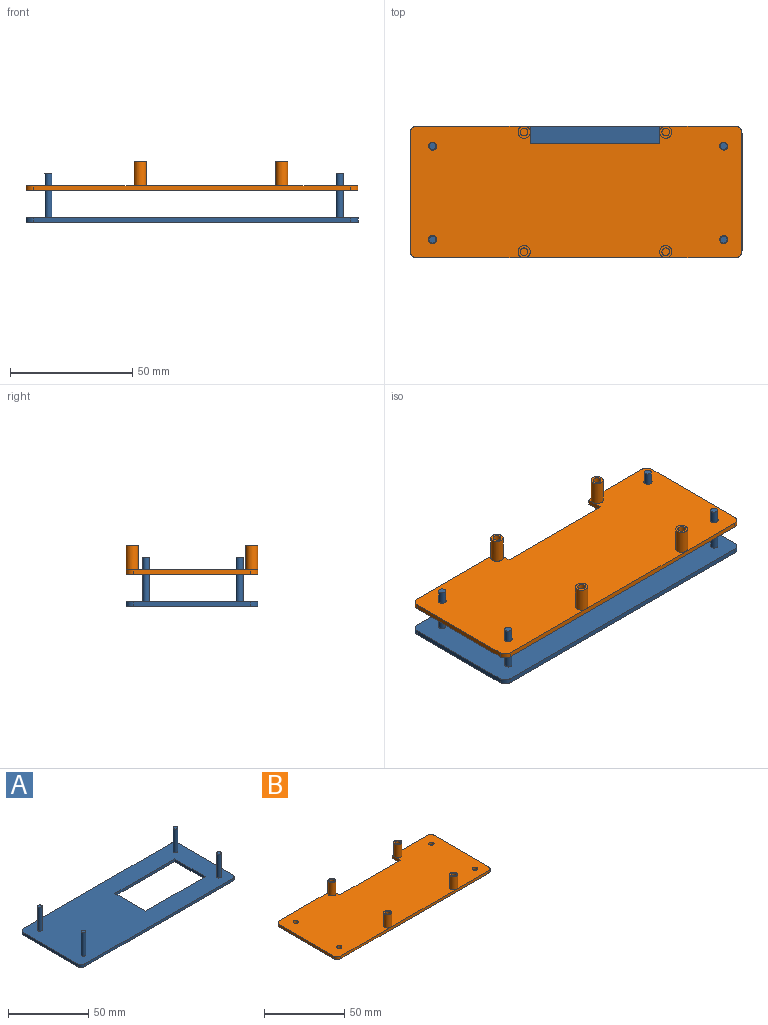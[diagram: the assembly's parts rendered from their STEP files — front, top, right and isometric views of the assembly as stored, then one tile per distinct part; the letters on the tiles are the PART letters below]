
ASSEMBLY  parts=2 mates=1
PART A: 22 faces, bbox 136x54x20 mm
  f0: plane 136x54mm, normal (0,0,1), area 5893.3mm2, adj f2,f3,f4,f5,f6,f8,f10,f12
  f1: plane 136x54mm, normal (0,0,-1), area 5918.8mm2, adj f2,f3,f4,f5,f14,f15,f16,f17
  f2: plane 130x2mm, normal (0,-1,0), area 260mm2, adj f0,f1,f18,f21
  f3: plane 48x2mm, normal (1,0,0), area 96mm2, adj f0,f1,f18,f19
  f4: plane 130x2mm, normal (0,1,0), area 260mm2, adj f0,f1,f19,f20
  f5: plane 48x2mm, normal (-1,0,0), area 96mm2, adj f0,f1,f20,f21
  f6: cylinder r=1.43mm len=18mm, axis (0,0,-1), area 161.2mm2, adj f0,f7
  f7: plane 2.85x2.85mm, normal (0,0,1), area 6.4mm2, adj f6
  f8: cylinder r=1.43mm len=18mm, axis (0,0,-1), area 161.2mm2, adj f0,f9
  f9: plane 2.85x2.85mm, normal (0,0,1), area 6.4mm2, adj f8
  f10: cylinder r=1.43mm len=18mm, axis (0,0,-1), area 161.2mm2, adj f0,f11
  f11: plane 2.85x2.85mm, normal (0,0,1), area 6.4mm2, adj f10
  f12: cylinder r=1.43mm len=18mm, axis (0,0,-1), area 161.2mm2, adj f0,f13
  f13: plane 2.85x2.85mm, normal (0,0,1), area 6.4mm2, adj f12
  f14: plane 52.5x2mm, normal (0,-1,0), area 105mm2, adj f0,f1,f15,f17
  f15: plane 27x2mm, normal (1,0,0), area 54mm2, adj f0,f1,f14,f16
  f16: plane 52.5x2mm, normal (0,1,0), area 105mm2, adj f0,f1,f15,f17
  f17: plane 27x2mm, normal (-1,0,0), area 54mm2, adj f0,f1,f14,f16
  f18: cylinder r=3mm len=3mm, axis (0,0,1), area 9.4mm2, adj f0,f1,f2,f3
  f19: cylinder r=3mm len=3mm, axis (0,0,-1), area 9.4mm2, adj f0,f1,f3,f4
  f20: cylinder r=3mm len=3mm, axis (0,0,1), area 9.4mm2, adj f0,f1,f4,f5
  f21: cylinder r=3mm len=3mm, axis (0,0,-1), area 9.4mm2, adj f0,f1,f2,f5
PART B: 36 faces, bbox 136x54x12 mm
  f0: plane 46.24x2mm, normal (0,1,0), area 92.5mm2, adj f1,f2,f3,f29,f34
  f1: plane 136x54mm, normal (0,0,1), area 6849.8mm2, adj f0,f5,f6,f7,f8,f10,f13,f18
  f2: plane 2.5x2.5mm, normal (0,0,1), area 1.3mm2, adj f0,f18,f29
  f3: plane 136x54mm, normal (0,0,-1), area 6931.1mm2, adj f0,f5,f6,f7,f8,f25,f26,f27
  f4: plane 2.5x2.5mm, normal (0,0,1), area 1.3mm2, adj f7,f13,f31
  f5: plane 130x2mm, normal (0,-1,0), area 260mm2, adj f1,f3,f32,f35
  f6: plane 48x2mm, normal (1,0,0), area 96mm2, adj f1,f3,f32,f33
  f7: plane 30.76x2mm, normal (0,1,0), area 61.5mm2, adj f1,f3,f4,f31,f33
  f8: plane 48x2mm, normal (-1,0,0), area 96mm2, adj f1,f3,f34,f35
  f9: cylinder r=1.57mm len=10mm, axis (0,0,-1), area 99mm2, adj f11,f12
  f10: cylinder r=2.5mm len=10mm, axis (0,0,-1), area 157.1mm2, adj f1,f11
  f11: plane 5x5mm, normal (0,0,1), area 11.8mm2, adj f9,f10
  f12: plane 3.15x3.15mm, normal (0,0,1), area 7.8mm2, adj f9
  f13: cylinder r=2.5mm len=10mm, axis (0,0,-1), area 157.1mm2, adj f1,f4,f15
  f14: cylinder r=1.57mm len=10mm, axis (0,0,-1), area 99mm2, adj f15,f16
  f15: plane 5x5mm, normal (0,0,1), area 11.8mm2, adj f13,f14
  f16: plane 3.15x3.15mm, normal (0,0,1), area 7.8mm2, adj f14
  f17: cylinder r=1.57mm len=10mm, axis (0,0,-1), area 99mm2, adj f19,f20
  f18: cylinder r=2.5mm len=10mm, axis (0,0,-1), area 157.1mm2, adj f1,f2,f19
  f19: plane 5x5mm, normal (0,0,1), area 11.8mm2, adj f17,f18
  f20: plane 3.15x3.15mm, normal (0,0,1), area 7.8mm2, adj f17
  f21: cylinder r=2.5mm len=10mm, axis (0,0,-1), area 157.1mm2, adj f1,f23
  f22: cylinder r=1.57mm len=10mm, axis (0,0,-1), area 99mm2, adj f23,f24
  f23: plane 5x5mm, normal (0,0,1), area 11.8mm2, adj f21,f22
  f24: plane 3.15x3.15mm, normal (0,0,1), area 7.8mm2, adj f22
  f25: cylinder r=1.65mm len=3.3mm, axis (0,0,1), area 20.7mm2, adj f1,f3
  f26: cylinder r=1.65mm len=3.3mm, axis (0,0,1), area 20.7mm2, adj f1,f3
  f27: cylinder r=1.65mm len=3.3mm, axis (0,0,1), area 20.7mm2, adj f1,f3
  f28: cylinder r=1.65mm len=3.3mm, axis (0,0,1), area 20.7mm2, adj f1,f3
  f29: plane 7x2mm, normal (1,0,0), area 14mm2, adj f0,f1,f2,f3,f30
  f30: plane 53x2mm, normal (0,1,0), area 106mm2, adj f1,f3,f29,f31
  f31: plane 7x2mm, normal (-1,0,0), area 14mm2, adj f1,f3,f4,f7,f30
  f32: cylinder r=3mm len=3mm, axis (0,0,1), area 9.4mm2, adj f1,f3,f5,f6
  f33: cylinder r=3mm len=3mm, axis (0,0,-1), area 9.4mm2, adj f1,f3,f6,f7
  f34: cylinder r=3mm len=3mm, axis (0,0,1), area 9.4mm2, adj f0,f1,f3,f8
  f35: cylinder r=3mm len=3mm, axis (0,0,-1), area 9.4mm2, adj f1,f3,f5,f8
PLACE A t=(-1.72,32.84,9.92)mm
PLACE B t=(0.73,66.01,22.92)mm
MATE pin_slot A.f6 <-> B.f28  axis (0,0,1) through (58.78,13.34,11.92)mm
